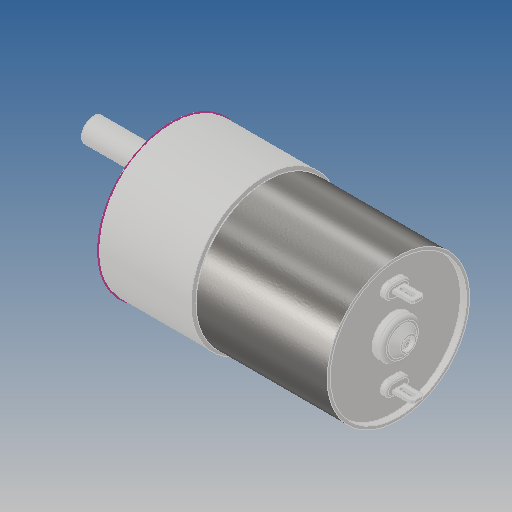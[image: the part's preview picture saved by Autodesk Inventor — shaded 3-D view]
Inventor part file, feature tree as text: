
AUTODESK INVENTOR PART (.ipt)
format: ipt  version: 2020 (Build 240168000, 168)  size: 285,696 bytes
history: native  units: mm
features: sketch x2, projected_geometry x2, extrude x1, other x1
ambient origin geometry x8: Origin, YZ Plane, XZ Plane, XY Plane, X Axis, Y Axis, Z Axis, Center Point
bodies: Solid1 (feature_tree)
feature tree (6):
  sketch  "Sketch1"  dims[d0=8.0mm d1=45.75mm d2=0.0mm]
  extrude  "Extrusion1"  Depth=45.75mm TaperAngle=0.0deg
  projected_geometry  "Projected Loop1"
  projected_geometry  "Projected Loop2"
  sketch  "Sketch2"
  other  "Aynalama2"
